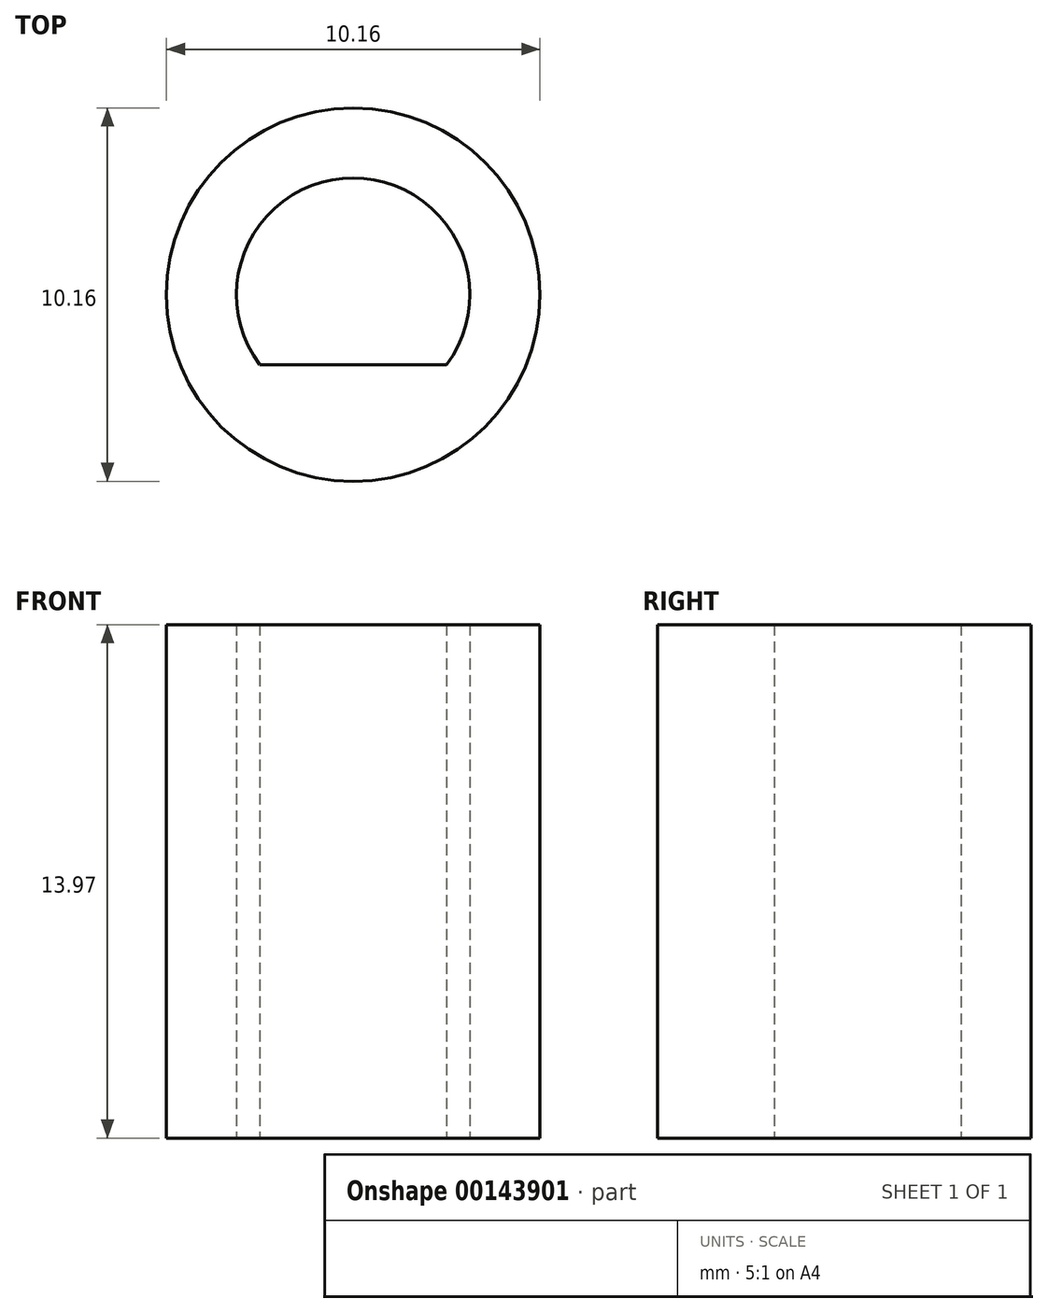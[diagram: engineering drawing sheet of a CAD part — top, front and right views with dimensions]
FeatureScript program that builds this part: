
annotation { "Feature Type Name" : "Feature", "Feature Type Description" : "" }
export const myFeature = defineFeature(function(context is Context, id is Id, definition is map)
    precondition{}
    {
        {
            var Q0;
            Q0=qCreatedBy(makeId("Top.planeOp"),FACE);
            var sketch = newSketch(context, id + "F0", { "sketchPlane" : qUnion([Q0])});
            skArc(sketch, "E0", {"start": v(1.88, 6.46) * mm, "mid": v(-0.66, 11.54) * mm, "end": v(-3.2, 6.46) * mm});
            skCircle(sketch, "E1", {"center": v(-0.66, 8.37) * mm, "radius": 5.08 * mm});
            skLineSegment(sketch, "E2", {"start": v(1.88, 6.46) * mm, "end": v(-3.2, 6.46) * mm});
            skPoint(sketch, "E3.orphan", {"position": v(-0.66, 11.54) * mm});
            skPoint(sketch, "E4.end.orphan", {"position": v(-0.66, 6.46) * mm});
            skSolve(sketch);
        }
        {
            var Q0;
            Q0=makeQuery(id+"F0.imprint","IMPRINT",FACE,{"disambiguationData":[TD([[makeQuery(id+"F0.imprint","IMPRINT",EDGE,{"derivedFrom":sQuery(id+"F0.wireOp",EDGE,"E0")}),-1.0]])]});
            extrude(context, id + "F1", {"entities" : qUnion([Q0]), "depth" : 13.97 * mm});
        }
    });
